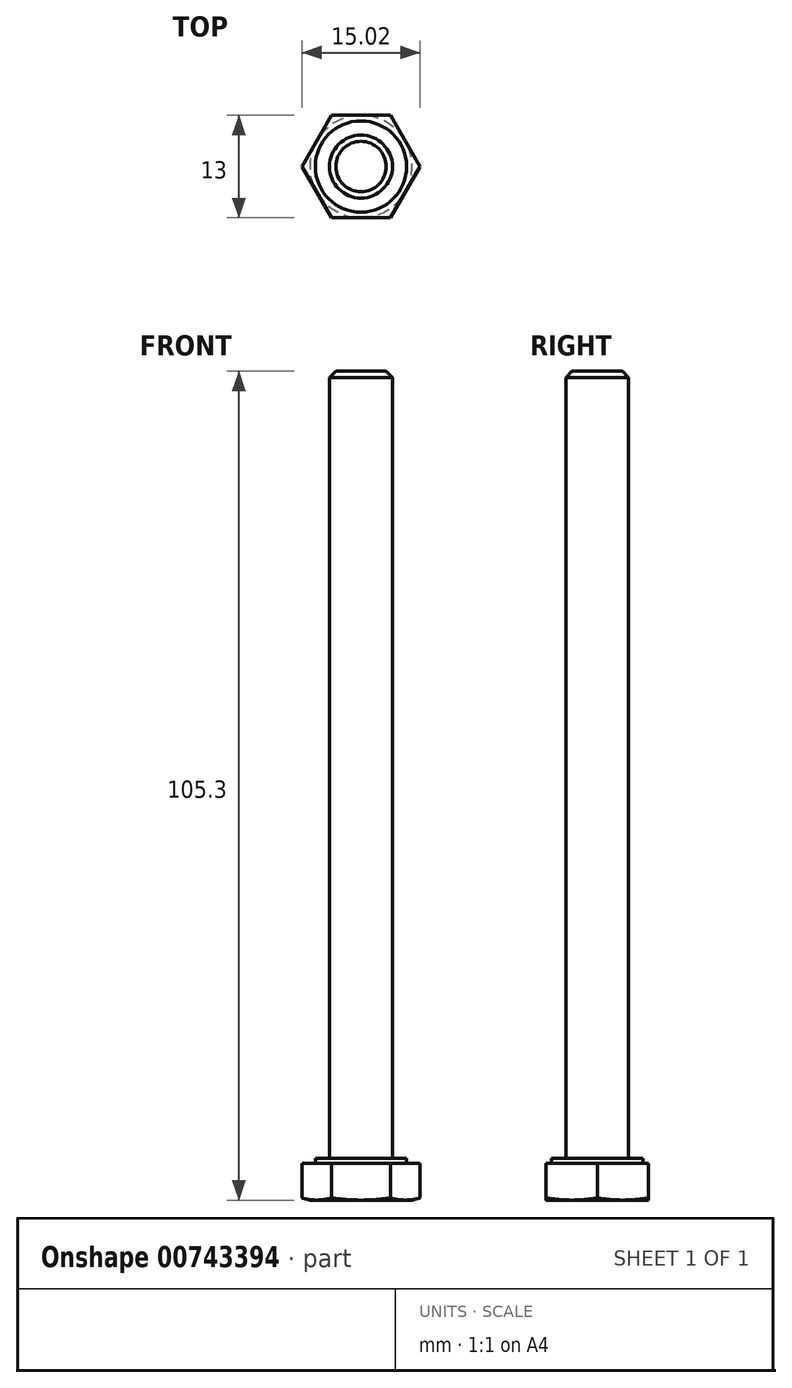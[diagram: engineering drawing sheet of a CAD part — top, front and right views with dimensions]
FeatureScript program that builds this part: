
annotation { "Feature Type Name" : "Feature", "Feature Type Description" : "" }
export const myFeature = defineFeature(function(context is Context, id is Id, definition is map)
    precondition{}
    {
        {
            var Q0;
            Q0=qCreatedBy(makeId("Top.planeOp"),FACE);
            var sketch = newSketch(context, id + "F0", { "sketchPlane" : qUnion([Q0])});
            skCircle(sketch, "E0.cCircle", {"center": v(0, 0) * mm, "radius": 6.5 * mm, "construction": true});
            skLineSegment(sketch, "E0.0", {"start": v(3.75, -6.5) * mm, "end": v(-3.75, -6.5) * mm});
            skLineSegment(sketch, "E0.1", {"start": v(-3.75, -6.5) * mm, "end": v(-7.5, 0) * mm});
            skLineSegment(sketch, "E0.2", {"start": v(-7.5, 0) * mm, "end": v(-3.75, 6.5) * mm});
            skLineSegment(sketch, "E0.3", {"start": v(-3.75, 6.5) * mm, "end": v(3.75, 6.5) * mm});
            skLineSegment(sketch, "E0.4", {"start": v(3.75, 6.5) * mm, "end": v(7.5, 0) * mm});
            skLineSegment(sketch, "E0.5", {"start": v(7.5, 0) * mm, "end": v(3.75, -6.5) * mm});
            skPoint(sketch, "E0.0.midPoint", {"position": v(0, -6.5) * mm});
            skSolve(sketch);
        }
        {
            var Q0;
            Q0 = qSketchRegion(id + "F0", true);
            extrude(context, id + "F1", {"entities" : qUnion([Q0]), "depth" : 4.7 * mm, "offsetDistance" : 25 * mm});
        }
        {
            var Q0;
            Q0=qCreatedBy(makeId("Front.planeOp"),FACE);
            var sketch = newSketch(context, id + "F2", { "sketchPlane" : qUnion([Q0])});
            skLineSegment(sketch, "E1", {"start": v(0, -11.74) * mm, "end": v(0, 32.47) * mm, "construction": true});
            skLineSegment(sketch, "E2", {"start": v(-6.5, 0) * mm, "end": v(-7.5, 0.27) * mm});
            skLineSegment(sketch, "E3", {"start": v(-7.5, 0.27) * mm, "end": v(-7.5, 0) * mm});
            skLineSegment(sketch, "E4", {"start": v(-7.5, 0) * mm, "end": v(-6.5, 0) * mm});
            skSolve(sketch);
        }
        {
            var Q0;
            Q0 = qSketchRegion(id + "F2", true);
            var Q1;
            Q1=sQuery(id+"F2.wireOp",EDGE,"E1");
            revolve(context, id + "F3", {"operationType" : NewBodyOperationType.REMOVE, "surfaceOperationType" : NewSurfaceOperationType.NEW, "entities" : qUnion([Q0]), "axis" : qUnion([Q1]), "revolveType" : RevolveType.FULL, "oppositeDirection" : true});
        }
        {
            var Q0;
            Q0=makeQuery(id+"F1.opExtrude","CAP_FACE",FACE,{"disambiguationData":[OSD([sQuery(id+"F0.wireOp",EDGE,"E0.0"),sQuery(id+"F0.wireOp",EDGE,"E0.1"),sQuery(id+"F0.wireOp",EDGE,"E0.2"),sQuery(id+"F0.wireOp",EDGE,"E0.3"),sQuery(id+"F0.wireOp",EDGE,"E0.4"),sQuery(id+"F0.wireOp",EDGE,"E0.5")])],"isStart":false});
            var sketch = newSketch(context, id + "F4", { "sketchPlane" : qUnion([Q0])});
            skCircle(sketch, "E5", {"center": v(0, 0) * mm, "radius": 5.8 * mm});
            skSolve(sketch);
        }
        {
            var Q0;
            Q0 = qSketchRegion(id + "F4", true);
            extrude(context, id + "F5", {"entities" : qUnion([Q0]), "operationType" : NewBodyOperationType.ADD, "depth" : 0.6 * mm, "offsetDistance" : 25 * mm});
        }
        {
            var Q0;
            Q0=makeQuery(id+"F5.opExtrude","CAP_FACE",FACE,{"disambiguationData":[OSD([sQuery(id+"F4.wireOp",EDGE,"E5")])],"isStart":false});
            var sketch = newSketch(context, id + "F6", { "sketchPlane" : qUnion([Q0])});
            skCircle(sketch, "E6", {"center": v(0, 0) * mm, "radius": 4 * mm});
            skSolve(sketch);
        }
        {
            var Q0;
            Q0 = qSketchRegion(id + "F6", true);
            extrude(context, id + "F7", {"entities" : qUnion([Q0]), "operationType" : NewBodyOperationType.ADD, "depth" : 100 * mm, "offsetDistance" : 25 * mm});
        }
        {
            var Q0;
            Q0=makeQuery(id+"F7.opExtrude","CAP_EDGE",EDGE,{"disambiguationData":[OSD([sQuery(id+"F6.wireOp",EDGE,"E6")])],"isStart":false});
            chamfer(context, id + "F8", {"entities" : qUnion([Q0]), "width" : 0.8 * mm, "tangentPropagation" : true});
        }
    });
